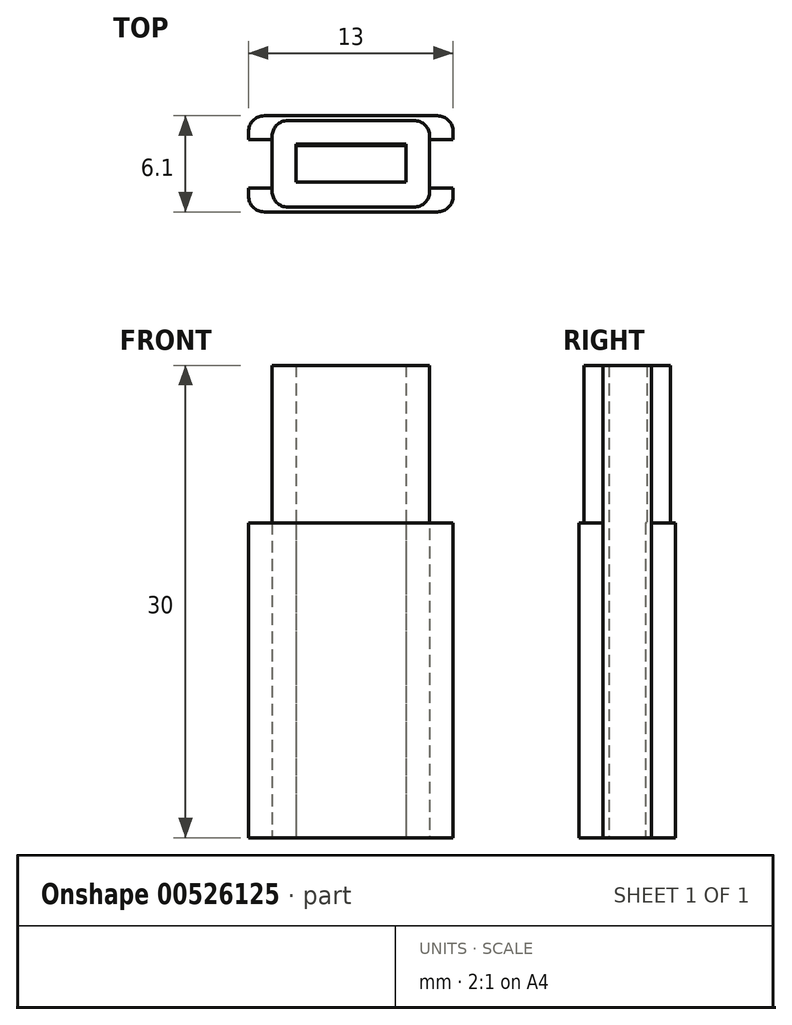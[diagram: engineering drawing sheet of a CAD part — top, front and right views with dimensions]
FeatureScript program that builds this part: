
annotation { "Feature Type Name" : "Feature", "Feature Type Description" : "" }
export const myFeature = defineFeature(function(context is Context, id is Id, definition is map)
    precondition{}
    {
        {
            var Q0;
            Q0=qCreatedBy(makeId("Top.planeOp"),FACE);
            var sketch = newSketch(context, id + "F0", { "sketchPlane" : qUnion([Q0])});
            skLineSegment(sketch, "E0", {"start": v(-6.5, 3.05) * mm, "end": v(6.5, 3.05) * mm});
            skLineSegment(sketch, "E1", {"start": v(6.5, 1.55) * mm, "end": v(5, 1.55) * mm});
            skLineSegment(sketch, "E2", {"start": v(5, 1.55) * mm, "end": v(5, -1.55) * mm});
            skLineSegment(sketch, "E3", {"start": v(5, -1.55) * mm, "end": v(6.5, -1.55) * mm});
            skLineSegment(sketch, "E4", {"start": v(6.5, -1.55) * mm, "end": v(6.5, -3.05) * mm});
            skLineSegment(sketch, "E5", {"start": v(6.5, -3.05) * mm, "end": v(-6.5, -3.05) * mm});
            skLineSegment(sketch, "E6", {"start": v(-6.5, -3.05) * mm, "end": v(-6.5, -1.55) * mm});
            skLineSegment(sketch, "E7", {"start": v(-6.5, -1.55) * mm, "end": v(-5, -1.55) * mm});
            skLineSegment(sketch, "E8", {"start": v(-5, -1.55) * mm, "end": v(-5, 1.55) * mm});
            skLineSegment(sketch, "E9", {"start": v(-5, 1.55) * mm, "end": v(-6.5, 1.55) * mm});
            skLineSegment(sketch, "E10", {"start": v(-6.5, 1.55) * mm, "end": v(-6.5, 3.05) * mm});
            skLineSegment(sketch, "E11", {"start": v(6.5, 3.05) * mm, "end": v(6.5, 1.55) * mm});
            skLineSegment(sketch, "E12.bottom", {"start": v(3.5, 1.15) * mm, "end": v(-3.5, 1.15) * mm});
            skLineSegment(sketch, "E12.top", {"start": v(3.5, -1.15) * mm, "end": v(-3.5, -1.15) * mm});
            skLineSegment(sketch, "E12.left", {"start": v(3.5, 1.15) * mm, "end": v(3.5, -1.15) * mm});
            skLineSegment(sketch, "E12.right", {"start": v(-3.5, 1.15) * mm, "end": v(-3.5, -1.15) * mm});
            skPoint(sketch, "E12.middle", {"position": v(0, 0) * mm});
            skSolve(sketch);
        }
        {
            var Q0;
            Q0=makeQuery(id+"F0.imprint","IMPRINT",FACE,{"disambiguationData":[TD([[makeQuery(id+"F0.imprint","IMPRINT",EDGE,{"derivedFrom":sQuery(id+"F0.wireOp",EDGE,"E0")}),-1.0]])]});
            extrude(context, id + "F1", {"entities" : qUnion([Q0]), "depth" : 20 * mm, "offsetDistance" : 25 * mm});
        }
        {
            var Q0;
            Q0=makeQuery(id+"F1.opExtrude","CAP_FACE",FACE,{"disambiguationData":[OSD([sQuery(id+"F0.wireOp",EDGE,"E0"),sQuery(id+"F0.wireOp",EDGE,"E1"),sQuery(id+"F0.wireOp",EDGE,"E2"),sQuery(id+"F0.wireOp",EDGE,"E3"),sQuery(id+"F0.wireOp",EDGE,"E4"),sQuery(id+"F0.wireOp",EDGE,"E5"),sQuery(id+"F0.wireOp",EDGE,"E6"),sQuery(id+"F0.wireOp",EDGE,"E7"),sQuery(id+"F0.wireOp",EDGE,"E8"),sQuery(id+"F0.wireOp",EDGE,"E9"),sQuery(id+"F0.wireOp",EDGE,"E10"),sQuery(id+"F0.wireOp",EDGE,"E11"),sQuery(id+"F0.wireOp",EDGE,"E12.bottom"),sQuery(id+"F0.wireOp",EDGE,"E12.top"),sQuery(id+"F0.wireOp",EDGE,"E12.left"),sQuery(id+"F0.wireOp",EDGE,"E12.right")])],"isStart":false});
            var sketch = newSketch(context, id + "F2", { "sketchPlane" : qUnion([Q0])});
            skLineSegment(sketch, "E13.bottom", {"start": v(-5, -2.75) * mm, "end": v(5, -2.75) * mm});
            skLineSegment(sketch, "E13.top", {"start": v(-5, 2.75) * mm, "end": v(5, 2.75) * mm});
            skLineSegment(sketch, "E13.left", {"start": v(-5, -2.75) * mm, "end": v(-5, 2.75) * mm});
            skLineSegment(sketch, "E13.right", {"start": v(5, -2.75) * mm, "end": v(5, 2.75) * mm});
            skLineSegment(sketch, "E14.bottom", {"start": v(-3.5, -1.15) * mm, "end": v(3.5, -1.15) * mm});
            skLineSegment(sketch, "E14.top", {"start": v(-3.5, 1.25) * mm, "end": v(3.5, 1.25) * mm});
            skLineSegment(sketch, "E14.left", {"start": v(-3.5, -1.15) * mm, "end": v(-3.5, 1.25) * mm});
            skLineSegment(sketch, "E14.right", {"start": v(3.5, -1.15) * mm, "end": v(3.5, 1.25) * mm});
            skSolve(sketch);
        }
        {
            var Q0;
            {var subQ4=sQuery(id+"F2.wireOp",EDGE,"E13.bottom");Q0=makeQuery(id+"F2.imprint","IMPRINT",FACE,{"disambiguationData":[TD([[makeQuery(id+"F2.imprint","IMPRINT",EDGE,{"derivedFrom":subQ4}),1.0]])]});}
            extrude(context, id + "F3", {"entities" : qUnion([Q0]), "operationType" : NewBodyOperationType.ADD, "depth" : 10 * mm, "offsetDistance" : 25 * mm});
        }
        {
            var Q0;
            Q0=makeQuery(id+"F3.opExtrude","SWEPT_EDGE",EDGE,{"disambiguationData":[OSD([sQuery(id+"F2.wireOp",EDGE,"E13.top"),sQuery(id+"F2.wireOp",EDGE,"E13.left")])]});
            var Q1;
            Q1=makeQuery(id+"F3.opExtrude","SWEPT_EDGE",EDGE,{"disambiguationData":[OSD([sQuery(id+"F2.wireOp",EDGE,"E13.bottom"),sQuery(id+"F2.wireOp",EDGE,"E13.left")])]});
            var Q2;
            Q2=makeQuery(id+"F3.opExtrude","SWEPT_EDGE",EDGE,{"disambiguationData":[OSD([sQuery(id+"F2.wireOp",EDGE,"E13.top"),sQuery(id+"F2.wireOp",EDGE,"E13.right")])]});
            var Q3;
            Q3=makeQuery(id+"F3.opExtrude","SWEPT_EDGE",EDGE,{"disambiguationData":[OSD([sQuery(id+"F2.wireOp",EDGE,"E13.bottom"),sQuery(id+"F2.wireOp",EDGE,"E13.right")])]});
            fillet(context, id + "F4", {"entities" : qUnion([Q0, Q1, Q2, Q3]), "radius" : 1 * mm, "tangentPropagation" : true, "allowEdgeOverflow" : false});
        }
        {
            var Q0;
            Q0=makeQuery(id+"F1.opExtrude","SWEPT_EDGE",EDGE,{"disambiguationData":[OSD([sQuery(id+"F0.wireOp",EDGE,"E0"),sQuery(id+"F0.wireOp",EDGE,"E10")])]});
            var Q1;
            Q1=makeQuery(id+"F1.opExtrude","SWEPT_EDGE",EDGE,{"disambiguationData":[OSD([sQuery(id+"F0.wireOp",EDGE,"E5"),sQuery(id+"F0.wireOp",EDGE,"E6")])]});
            var Q2;
            Q2=makeQuery(id+"F1.opExtrude","SWEPT_EDGE",EDGE,{"disambiguationData":[OSD([sQuery(id+"F0.wireOp",EDGE,"E0"),sQuery(id+"F0.wireOp",EDGE,"E11")])]});
            var Q3;
            Q3=makeQuery(id+"F1.opExtrude","SWEPT_EDGE",EDGE,{"disambiguationData":[OSD([sQuery(id+"F0.wireOp",EDGE,"E4"),sQuery(id+"F0.wireOp",EDGE,"E5")])]});
            fillet(context, id + "F5", {"entities" : qUnion([Q0, Q1, Q2, Q3]), "radius" : 1 * mm, "tangentPropagation" : true, "allowEdgeOverflow" : false});
        }
    });
